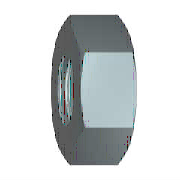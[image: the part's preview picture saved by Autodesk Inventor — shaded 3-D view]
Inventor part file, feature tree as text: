
AUTODESK INVENTOR PART (.ipt)
format: ipt  version: 2017 (Build 210142000, 142)  size: 173,568 bytes
history: native  units: mm (DEFAULTED — no unit token found)
features: sketch x3, chamfer x1, hole x1, other x1, plane x1
ambient origin geometry x7: Origin, YZ Plane, XZ Plane, X Axis, Y Axis, Z Axis, Center Point
bodies: Solid1 (feature_tree), Body (feature_tree)
feature tree (7):
  chamfer  "Chamfer1"  Angle=30.0deg  [1 undecoded]
  hole  "Thread"  [1 undecoded]
  other  "Work Axis1"
  plane  "Work Plane1"
  sketch  "Sketch1"  dims[d0=9.237604mm]
  sketch  "Sketch2"  dims[d1=5.1mm]
  sketch  "Sketch3"  dims[d2=0.0mm d3=30.0deg d4=30.0deg d5=8.0mm d6=8.0mm d7=90.0deg d25=4.134mm d26=6.0mm d27=4.0mm d28=2.0mm d29=14.3117mm d30=8.0mm d31=20.594885mm d8=0.433013mm d9=30.0deg d10=0.433013mm d11=30.0deg d13=0.0mm d14=0.0mm d39=0.0mm d40=0.433013mm d41=0.433013mm d42=0.0mm]
note: 2 required parameter values undecoded (feature->parameter linkage not recoverable at this tier; creation-order binding heuristic only, values carry confidence <= 0.55)
